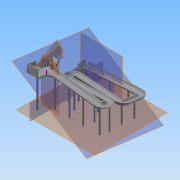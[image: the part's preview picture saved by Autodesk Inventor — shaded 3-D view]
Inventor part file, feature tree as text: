
AUTODESK INVENTOR PART (.ipt)
format: ipt  version: 2015 (Build 190159000, 159)  size: 1,350,656 bytes
history: native  units: mm
features: sketch x35, extrude x17, plane x15, sweep x5, other x4, fillet x2, projected_geometry x2, loft x1
ambient origin geometry x8: Origin, YZ Plane, XZ Plane, XY Plane, X Axis, Y Axis, Z Axis, Center Point
bodies: Body1 (feature_tree)
feature tree (81):
  other  "實體1"
  extrude  "擠出1"  Depth=12.0mm
  plane  "工作平面1"
  sketch  "草圖2"
  sketch  "草圖3"
  plane  "工作平面3"
  plane  "工作平面4"
  extrude  "擠出5"  Depth=14.0mm
  plane  "工作平面5"
  sketch  "草圖9"
  sketch  "草圖10"
  plane  "工作平面7"
  sweep  "掃掠2"
  plane  "工作平面8"
  extrude  "擠出7"  Depth=5.0mm TaperAngle=0.0deg
  extrude  "擠出8"  Depth=2.0mm
  plane  "工作平面10"
  sweep  "掃掠3"
  sketch  "草圖15"
  sweep  "掃掠4"
  sketch  "草圖18"
  sweep  "掃掠5"
  plane  "工作平面11"
  extrude  "擠出9"  TaperAngle=0.0deg  [1 undecoded]
  fillet  "圓角1"  [1 undecoded]
  sweep  "掃掠6"
  loft  "斷面混成1"
  fillet  "圓角2"  Radius=10.0mm
  plane  "工作平面12"
  extrude  "擠出10"  Depth=10.0mm
  extrude  "擠出11"  Depth=10.0mm
  sketch  "草圖25"
  plane  "工作平面13"
  extrude  "擠出12"  Depth=10.0mm
  extrude  "擠出13"  Depth=10.0mm
  extrude  "擠出14"  TaperAngle=0.0deg  [1 undecoded]
  extrude  "擠出15"  Depth=12.5mm TaperAngle=0.0deg
  other  "迴轉1"
  extrude  "擠出16"  Depth=20.0mm
  extrude  "擠出17"  TaperAngle=0.0deg  [1 undecoded]
  extrude  "擠出18"  TaperAngle=0.0deg  [1 undecoded]
  extrude  "擠出19"  TaperAngle=0.0deg  [1 undecoded]
  plane  "工作平面14"
  sketch  "草圖34"
  extrude  "擠出20"  Depth=2.0mm
  plane  "工作平面15"
  extrude  "擠出21"  Depth=3.0mm
  sketch  "3D 草圖1"
  sketch  "草圖1"
  other  "參考1"
  projected_geometry  "投影迴路1"
  plane  "工作平面2"
  sketch  "草圖8"
  other  "參考2"
  plane  "工作平面6"
  sketch  "草圖11"
  sketch  "草圖12"
  projected_geometry  "投影迴路3"
  sketch  "草圖13"
  plane  "工作平面9"
  sketch  "草圖14"
  sketch  "草圖16"
  sketch  "草圖17"
  sketch  "草圖19"
  sketch  "3D 草圖2"
  sketch  "草圖20"
  sketch  "草圖21"
  sketch  "3D 草圖3"
  sketch  "草圖22"
  sketch  "草圖23"
  sketch  "草圖24"
  sketch  "草圖26"
  sketch  "草圖27"
  sketch  "草圖28"
  sketch  "草圖29"
  sketch  "草圖30"
  sketch  "草圖31"
  sketch  "草圖32"
  sketch  "草圖33"
  sketch  "草圖35"
  sketch  "草圖36"
note: 6 required parameter values undecoded (feature->parameter linkage not recoverable at this tier; creation-order binding heuristic only, values carry confidence <= 0.55)
